# Revit family: SYSIMPLE FCS100A
name_source: partatom
category: Обобщенные модели
units: mm (PartAtom-declared; Revit-internal decimal feet)

## family parameters
Всегда вертикально = Да
Может служить основой для арматурных стержней = Нет
На основе рабочей плоскости = Нет
Общий = Нет
При загрузке вырезать с полостями = Нет
Размер круглого соединителя = Использовать диаметр
Тип детали = Нормальный
Точка расчета площади = Нет

## types (1)
- SYSIMPLE FCS100A
    Air guide size(mm) = /
    Body dimension(W) = 835×835×290
    COP = /
    Capacity = /
    Chassis height（mm) = /
    Compressor quantity = /
    Compressor type = /
    Cooling Power input = /
    Cooling capacity = 10810/9189/7027
    Cooling current = /
    Current of Circuit breaker = /
    Design Pressure(Mpa） = 1.6
    EER = /
    Fan motor quantity = /
    Gross Weight（body/panel） = 37/7
    Heating capacity = 16250/13774/10553
    Heating current = /
    Heating power input = /
    Inlet/Outlet /Drain  Water Pipe = DN20
    Installation hole spacing（L) = 510.4*514.6*530.5*463
    Installation hole spacing（W) = /
    Left Side clearance(ODU side mm) = /
    Manufacturer = AUX
    Manufacturer URL = /
    Max.Current input = /
    Max.Power input = /
    Model = AFC-1200CA/4BA
    NET Weight（body/panel） = 30/5
    Noise Level(dB) = ≤50
    ODU fan ESP = /
    Operation range Heatling (°C） = /
    Operation range cooling (°C） = /
    Power = 220-240V,50,1
    Product series = Cassette FCU
    Protection grade = /
    Refrigerant Charged Volume(kg) = R410a
    Refrigerant type = /
    Right Side clearance(ODU side mm) = /
    fan type = AC
    panel dimension(W) = 950x950x55
